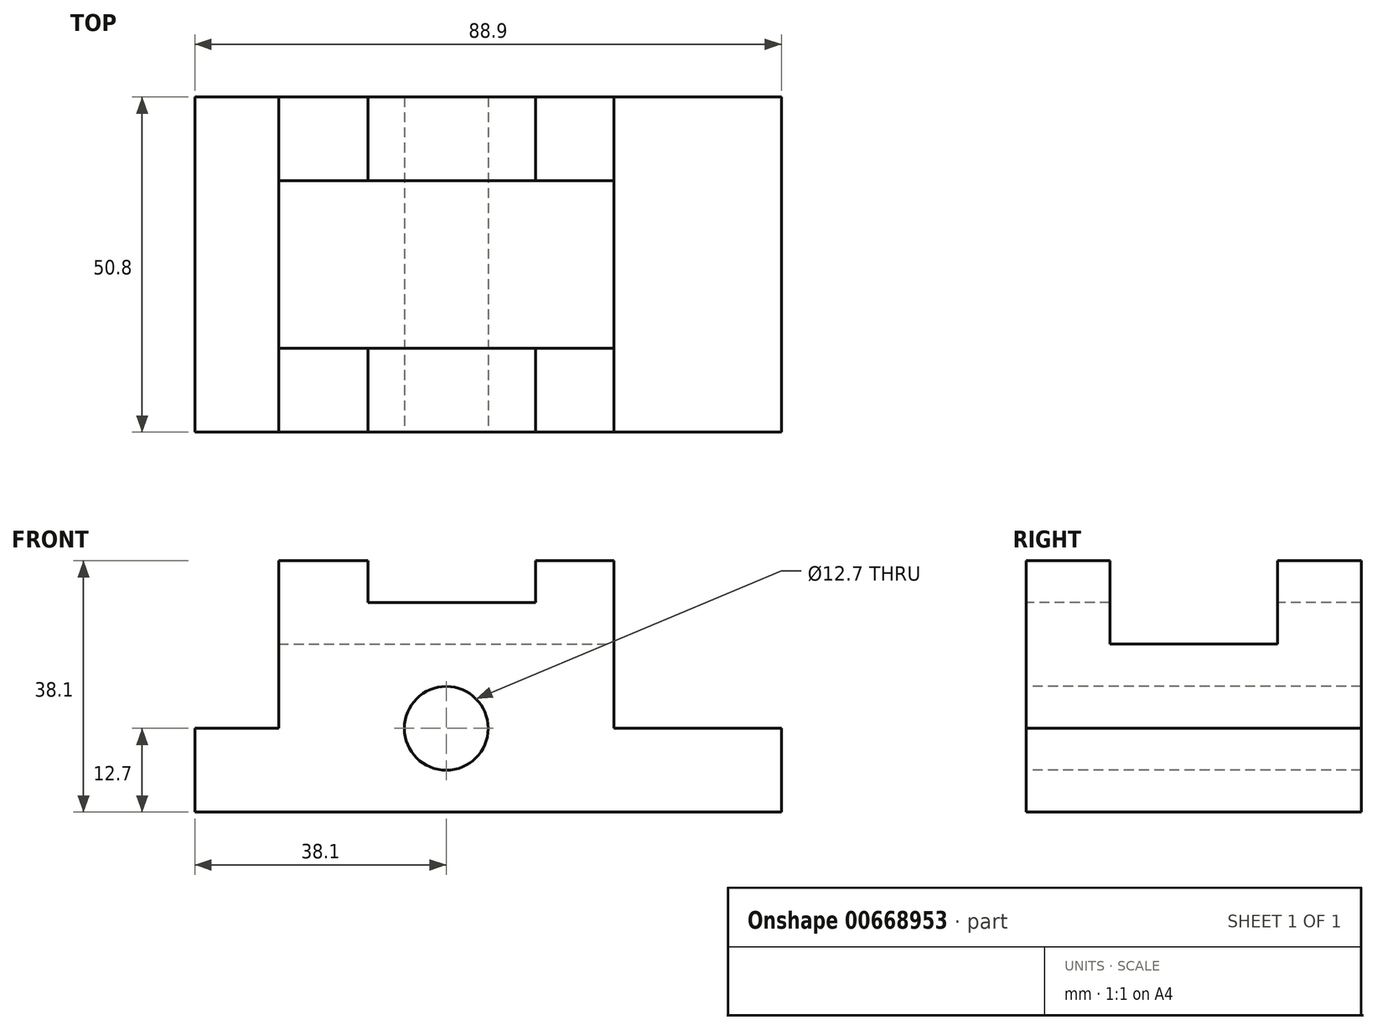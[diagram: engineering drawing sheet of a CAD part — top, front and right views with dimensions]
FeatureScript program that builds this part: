
annotation { "Feature Type Name" : "Feature", "Feature Type Description" : "" }
export const myFeature = defineFeature(function(context is Context, id is Id, definition is map)
    precondition{}
    {
        {
            var Q0;
            Q0=qCreatedBy(makeId("Front.planeOp"),FACE);
            var sketch = newSketch(context, id + "F0", { "sketchPlane" : qUnion([Q0])});
            skLineSegment(sketch, "E0.bottom", {"start": v(-44.45, -19.05) * mm, "end": v(44.45, -19.05) * mm});
            skLineSegment(sketch, "E0.top", {"start": v(-44.45, 19.05) * mm, "end": v(44.45, 19.05) * mm});
            skLineSegment(sketch, "E0.left", {"start": v(-44.45, -19.05) * mm, "end": v(-44.45, 19.05) * mm});
            skLineSegment(sketch, "E0.right", {"start": v(44.45, -19.05) * mm, "end": v(44.45, 19.05) * mm});
            skPoint(sketch, "E0.middle", {"position": v(0, 0) * mm});
            skSolve(sketch);
        }
        {
            var Q0;
            Q0 = qSketchRegion(id + "F0", true);
            extrude(context, id + "F1", {"entities" : qUnion([Q0]), "depth" : 50.8 * mm, "offsetDistance" : 25.4 * mm});
        }
        {
            var Q0;
            Q0=makeQuery(id+"F1.opExtrude","CAP_FACE",FACE,{"disambiguationData":[OSD([sQuery(id+"F0.wireOp",EDGE,"E0.bottom"),sQuery(id+"F0.wireOp",EDGE,"E0.top"),sQuery(id+"F0.wireOp",EDGE,"E0.left"),sQuery(id+"F0.wireOp",EDGE,"E0.right")])],"isStart":false});
            var sketch = newSketch(context, id + "F2", { "sketchPlane" : qUnion([Q0])});
            skLineSegment(sketch, "E1.bottom", {"start": v(-44.45, 19.05) * mm, "end": v(-31.75, 19.05) * mm});
            skLineSegment(sketch, "E1.top", {"start": v(-44.45, -6.35) * mm, "end": v(-31.75, -6.35) * mm});
            skLineSegment(sketch, "E1.left", {"start": v(-44.45, 19.05) * mm, "end": v(-44.45, -6.35) * mm});
            skLineSegment(sketch, "E1.right", {"start": v(-31.75, 19.05) * mm, "end": v(-31.75, -6.35) * mm});
            skSolve(sketch);
        }
        {
            var Q0;
            Q0 = qSketchRegion(id + "F2", true);
            extrude(context, id + "F3", {"entities" : qUnion([Q0]), "operationType" : NewBodyOperationType.REMOVE, "endBound" : BoundingType.THROUGH_ALL, "oppositeDirection" : true, "depth" : 25.4 * mm, "offsetDistance" : 25.4 * mm});
        }
        {
            var Q0;
            Q0=makeQuery(id+"F1.opExtrude","CAP_FACE",FACE,{"disambiguationData":[OSD([sQuery(id+"F0.wireOp",EDGE,"E0.bottom"),sQuery(id+"F0.wireOp",EDGE,"E0.top"),sQuery(id+"F0.wireOp",EDGE,"E0.left"),sQuery(id+"F0.wireOp",EDGE,"E0.right")])],"isStart":false});
            var sketch = newSketch(context, id + "F4", { "sketchPlane" : qUnion([Q0])});
            skLineSegment(sketch, "E2.bottom", {"start": v(44.45, 19.05) * mm, "end": v(19.05, 19.05) * mm});
            skLineSegment(sketch, "E2.top", {"start": v(44.45, -6.35) * mm, "end": v(19.05, -6.35) * mm});
            skLineSegment(sketch, "E2.left", {"start": v(44.45, 19.05) * mm, "end": v(44.45, -6.35) * mm});
            skLineSegment(sketch, "E2.right", {"start": v(19.05, 19.05) * mm, "end": v(19.05, -6.35) * mm});
            skSolve(sketch);
        }
        {
            var Q0;
            Q0 = qSketchRegion(id + "F4", true);
            extrude(context, id + "F5", {"entities" : qUnion([Q0]), "operationType" : NewBodyOperationType.REMOVE, "endBound" : BoundingType.THROUGH_ALL, "oppositeDirection" : true, "depth" : 25.4 * mm, "offsetDistance" : 25.4 * mm});
        }
        {
            var Q0;
            Q0=makeQuery(id+"F1.opExtrude","CAP_FACE",FACE,{"disambiguationData":[OSD([sQuery(id+"F0.wireOp",EDGE,"E0.bottom"),sQuery(id+"F0.wireOp",EDGE,"E0.top"),sQuery(id+"F0.wireOp",EDGE,"E0.left"),sQuery(id+"F0.wireOp",EDGE,"E0.right")])],"isStart":false});
            var sketch = newSketch(context, id + "F6", { "sketchPlane" : qUnion([Q0])});
            skLineSegment(sketch, "E3.bottom", {"start": v(-18.2, 19.05) * mm, "end": v(7.2, 19.05) * mm});
            skLineSegment(sketch, "E3.top", {"start": v(-18.2, 12.7) * mm, "end": v(7.2, 12.7) * mm});
            skLineSegment(sketch, "E3.left", {"start": v(-18.2, 19.05) * mm, "end": v(-18.2, 12.7) * mm});
            skLineSegment(sketch, "E3.right", {"start": v(7.2, 19.05) * mm, "end": v(7.2, 12.7) * mm});
            skPoint(sketch, "E3.middle", {"position": v(-5.5, 15.88) * mm});
            skSolve(sketch);
        }
        {
            var Q0;
            Q0 = qSketchRegion(id + "F6", true);
            extrude(context, id + "F7", {"entities" : qUnion([Q0]), "operationType" : NewBodyOperationType.REMOVE, "endBound" : BoundingType.THROUGH_ALL, "oppositeDirection" : true, "depth" : 25.4 * mm, "offsetDistance" : 25.4 * mm});
        }
        {
            var Q0;
            Q0=makeQuery(id+"F1.opExtrude","CAP_FACE",FACE,{"disambiguationData":[OSD([sQuery(id+"F0.wireOp",EDGE,"E0.bottom"),sQuery(id+"F0.wireOp",EDGE,"E0.top"),sQuery(id+"F0.wireOp",EDGE,"E0.left"),sQuery(id+"F0.wireOp",EDGE,"E0.right")])],"isStart":false});
            var sketch = newSketch(context, id + "F8", { "sketchPlane" : qUnion([Q0])});
            skCircle(sketch, "E4", {"center": v(-6.35, -6.35) * mm, "radius": 6.35 * mm});
            skSolve(sketch);
        }
        {
            var Q0;
            Q0 = qSketchRegion(id + "F8", true);
            extrude(context, id + "F9", {"entities" : qUnion([Q0]), "operationType" : NewBodyOperationType.REMOVE, "endBound" : BoundingType.THROUGH_ALL, "oppositeDirection" : true, "depth" : 25.4 * mm, "offsetDistance" : 25.4 * mm});
        }
        {
            var Q0;
            Q0=makeQuery(id+"F5.boolean.opBoolean","COPY",FACE,{"derivedFrom":makeQuery(id+"F5.opExtrude","SWEPT_FACE",FACE,{"disambiguationData":[OSD([sQuery(id+"F4.wireOp",EDGE,"E2.right")])]})});
            var sketch = newSketch(context, id + "F10", { "sketchPlane" : qUnion([Q0])});
            skLineSegment(sketch, "E5.bottom", {"start": v(-38.1, 6.43) * mm, "end": v(-12.7, 6.43) * mm});
            skLineSegment(sketch, "E5.top", {"start": v(-38.1, 19.13) * mm, "end": v(-12.7, 19.13) * mm});
            skLineSegment(sketch, "E5.left", {"start": v(-38.1, 6.43) * mm, "end": v(-38.1, 19.13) * mm});
            skLineSegment(sketch, "E5.right", {"start": v(-12.7, 6.43) * mm, "end": v(-12.7, 19.13) * mm});
            skPoint(sketch, "E5.middle", {"position": v(-25.4, 12.78) * mm});
            skPoint(sketch, "E5.middle.positionSnap0", {"position": v(-25.4, 19.05) * mm});
            skPoint(sketch, "E5.centerSnap0", {"position": v(-25.4, 19.05) * mm});
            skSolve(sketch);
        }
        {
            var Q0;
            Q0 = qSketchRegion(id + "F10", true);
            extrude(context, id + "F11", {"entities" : qUnion([Q0]), "operationType" : NewBodyOperationType.REMOVE, "endBound" : BoundingType.THROUGH_ALL, "oppositeDirection" : true, "depth" : 25.4 * mm, "offsetDistance" : 25.4 * mm});
        }
    });
